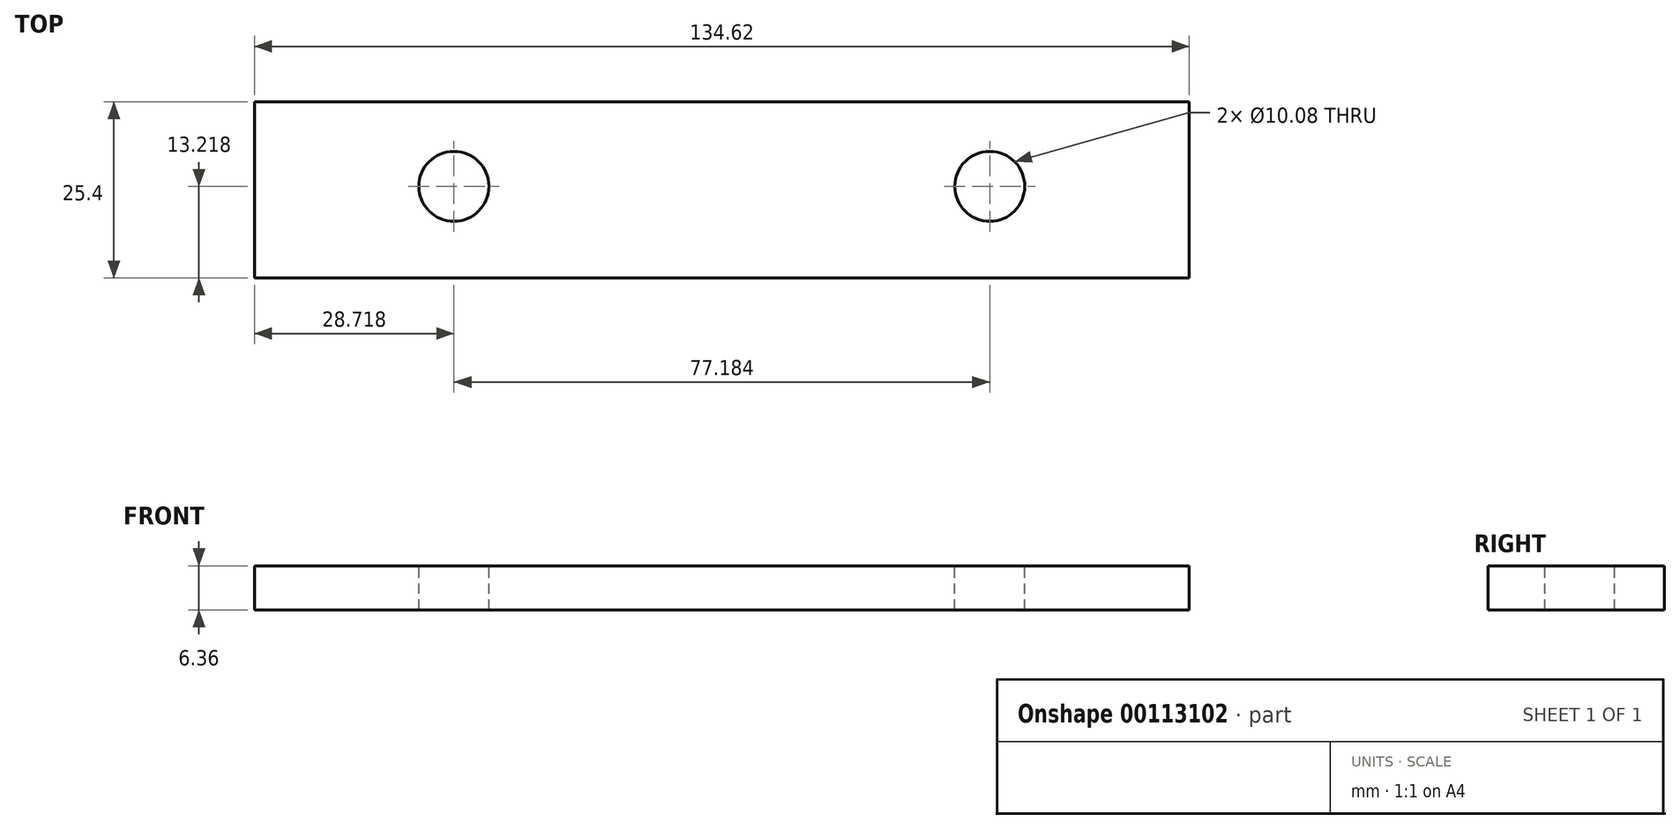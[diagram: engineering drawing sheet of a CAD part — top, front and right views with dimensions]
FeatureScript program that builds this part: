
annotation { "Feature Type Name" : "Feature", "Feature Type Description" : "" }
export const myFeature = defineFeature(function(context is Context, id is Id, definition is map)
    precondition{}
    {
        {
            var Q0;
            Q0=qCreatedBy(makeId("Front.planeOp"),FACE);
            var sketch = newSketch(context, id + "F0", { "sketchPlane" : qUnion([Q0])});
            skLineSegment(sketch, "E0.bottom", {"start": v(67.3, -3.18) * mm, "end": v(-67.31, -3.18) * mm});
            skLineSegment(sketch, "E0.top", {"start": v(67.31, 3.17) * mm, "end": v(-67.31, 3.17) * mm});
            skLineSegment(sketch, "E0.left", {"start": v(67.3, -3.18) * mm, "end": v(67.3, 3.17) * mm});
            skLineSegment(sketch, "E0.right", {"start": v(-67.31, -3.18) * mm, "end": v(-67.31, 3.17) * mm});
            skPoint(sketch, "E0.middle", {"position": v(0, 0) * mm});
            skLineSegment(sketch, "E1.bottom", {"start": v(67.31, 3.17) * mm, "end": v(60.96, 3.17) * mm});
            skLineSegment(sketch, "E1.top", {"start": v(67.3, 412.15) * mm, "end": v(60.96, 412.15) * mm});
            skLineSegment(sketch, "E1.left", {"start": v(67.31, 3.17) * mm, "end": v(67.3, 412.15) * mm});
            skLineSegment(sketch, "E1.right", {"start": v(60.96, 3.17) * mm, "end": v(60.96, 412.15) * mm});
            skLineSegment(sketch, "E2.bottom", {"start": v(-67.31, 3.17) * mm, "end": v(-60.96, 3.17) * mm});
            skLineSegment(sketch, "E2.top", {"start": v(-67.31, 407.03) * mm, "end": v(-60.96, 407.03) * mm});
            skLineSegment(sketch, "E2.left", {"start": v(-67.3, 3.17) * mm, "end": v(-67.31, 407.03) * mm});
            skLineSegment(sketch, "E2.right", {"start": v(-60.96, 3.17) * mm, "end": v(-60.96, 407.03) * mm});
            skSolve(sketch);
        }
        {
            var Q0;
            Q0=makeQuery(id+"F0.imprint","IMPRINT",FACE,{"disambiguationData":[TD([[makeQuery(id+"F0.imprint","IMPRINT",EDGE,{"derivedFrom":sQuery(id+"F0.wireOp",EDGE,"E2.bottom")}),1.0]])]});
            var Q1;
            Q1=makeQuery(id+"F0.imprint","IMPRINT",FACE,{"disambiguationData":[TD([[makeQuery(id+"F0.imprint","IMPRINT",EDGE,{"derivedFrom":sQuery(id+"F0.wireOp",EDGE,"E1.bottom")}),-1.0]])]});
            var Q2;
            Q2=makeQuery(id+"F0.imprint","IMPRINT",FACE,{"disambiguationData":[TD([[makeQuery(id+"F0.imprint","IMPRINT",EDGE,{"derivedFrom":sQuery(id+"F0.wireOp",EDGE,"E0.bottom")}),-1.0]])]});
            extrude(context, id + "F1", {"entities" : qUnion([Q0, Q1, Q2]), "depth" : 25.4 * mm});
        }
        {
            var Q0;
            Q0=makeQuery(id+"F1.opExtrude","SWEPT_FACE",FACE,{"disambiguationData":[OSD([sQuery(id+"F0.wireOp",EDGE,"E0.bottom")])]});
            var sketch = newSketch(context, id + "F2", { "sketchPlane" : qUnion([Q0])});
            skCircle(sketch, "E3", {"center": v(-38.6, 12.18) * mm, "radius": 5 * mm});
            skCircle(sketch, "E4.MirrorC", {"center": v(38.6, 12.18) * mm, "radius": 5 * mm});
            skSolve(sketch);
        }
        {
            var Q0;
            Q0=sQuery(id+"F2.wireOp",VERTEX,"E3.center");
            var Q1;
            Q1=sQuery(id+"F2.wireOp",VERTEX,"E4.MirrorC.center");
            var Q2;
            Q2=makeQuery(id+"F1.opExtrude","SWEPT_BODY",BODY,{"disambiguationData":[OSD([sQuery(id+"F0.wireOp",EDGE,"E0.bottom"),sQuery(id+"F0.wireOp",EDGE,"E0.top"),sQuery(id+"F0.wireOp",EDGE,"E0.left"),sQuery(id+"F0.wireOp",EDGE,"E0.right"),sQuery(id+"F0.wireOp",EDGE,"E1.top"),sQuery(id+"F0.wireOp",EDGE,"E1.left"),sQuery(id+"F0.wireOp",EDGE,"E1.right"),sQuery(id+"F0.wireOp",EDGE,"E2.top"),sQuery(id+"F0.wireOp",EDGE,"E2.left"),sQuery(id+"F0.wireOp",EDGE,"E2.right")])]});
            hole(context, id + "F3", {"style" : HoleStyle.SIMPLE, "endStyle" : HoleEndStyle.THROUGH, "standardTappedOrClearance" : lookupTablePath({ "standard" : "ANSI", "fit" : "Normal (ASME)", "size" : "3/8", "type" : "Clearance" }), "standardBlindInLast" : lookupTablePath({ "fit" : "Free", "standard" : "ANSI", "size" : "3/8", "type" : "Clearance" }), "holeDiameter" : 10.08 * mm, "locations" : qUnion([Q0, Q1]), "scope" : qUnion([Q2]), "isTappedThrough" : true, "startStyle" : HoleStartStyle.SKETCH});
        }
    });
